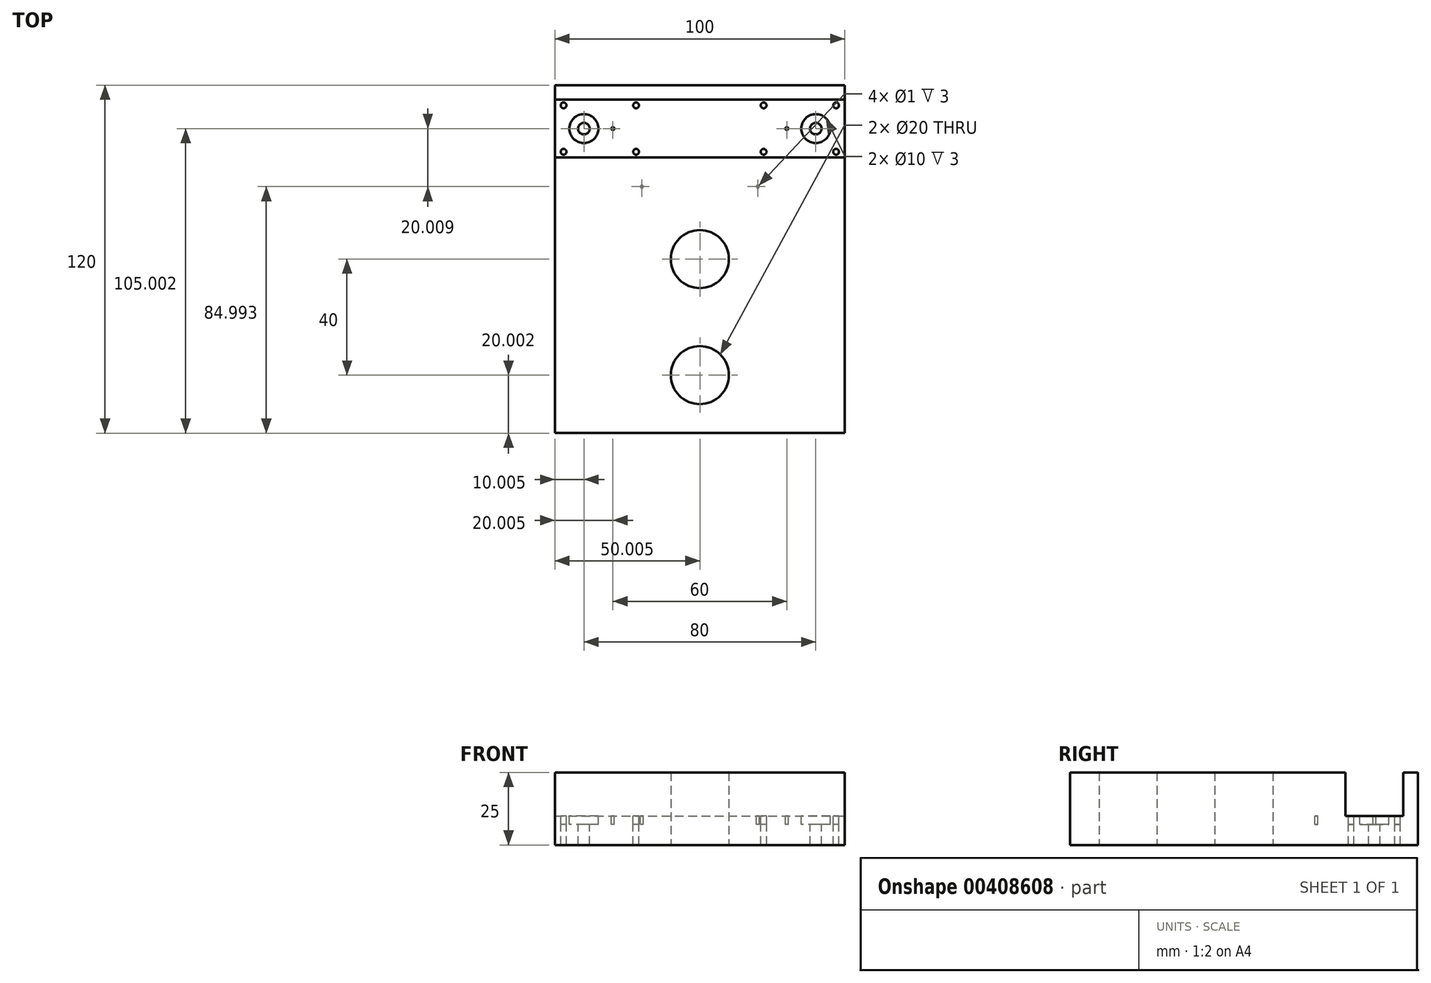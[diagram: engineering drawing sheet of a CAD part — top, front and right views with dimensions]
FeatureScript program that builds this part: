
annotation { "Feature Type Name" : "Feature", "Feature Type Description" : "" }
export const myFeature = defineFeature(function(context is Context, id is Id, definition is map)
    precondition{}
    {
        {
            var Q0;
            Q0=qCreatedBy(makeId("Top.planeOp"),FACE);
            var sketch = newSketch(context, id + "F0", { "sketchPlane" : qUnion([Q0])});
            skLineSegment(sketch, "E0.bottom", {"start": v(-65.16, 65.34) * mm, "end": v(34.84, 65.34) * mm});
            skLineSegment(sketch, "E0.top", {"start": v(-65.16, -54.66) * mm, "end": v(34.84, -54.66) * mm});
            skLineSegment(sketch, "E0.left", {"start": v(-65.16, 65.34) * mm, "end": v(-65.16, -54.66) * mm});
            skLineSegment(sketch, "E0.right", {"start": v(34.84, 65.34) * mm, "end": v(34.84, -54.66) * mm});
            skLineSegment(sketch, "E1", {"start": v(-15.16, 65.34) * mm, "end": v(-15.16, -54.66) * mm, "construction": true});
            skCircle(sketch, "E2", {"center": v(-15.16, 5.34) * mm, "radius": 10 * mm});
            skCircle(sketch, "E3", {"center": v(-15.16, -34.66) * mm, "radius": 10 * mm});
            skSolve(sketch);
        }
        {
            var Q0;
            Q0=makeQuery(id+"F0.imprint","IMPRINT",FACE,{"disambiguationData":[TD([[makeQuery(id+"F0.imprint","IMPRINT",EDGE,{"derivedFrom":sQuery(id+"F0.wireOp",EDGE,"E0.bottom")}),-1.0]])]});
            extrude(context, id + "F1", {"entities" : qUnion([Q0]), "depth" : 25 * mm});
        }
        {
            var Q0;
            Q0=makeQuery(id+"F1.opExtrude","CAP_FACE",FACE,{"disambiguationData":[OSD([sQuery(id+"F0.wireOp",EDGE,"E0.bottom"),sQuery(id+"F0.wireOp",EDGE,"E0.top"),sQuery(id+"F0.wireOp",EDGE,"E0.left"),sQuery(id+"F0.wireOp",EDGE,"E0.right"),sQuery(id+"F0.wireOp",EDGE,"E2"),sQuery(id+"F0.wireOp",EDGE,"E3")])],"isStart":false});
            var sketch = newSketch(context, id + "F2", { "sketchPlane" : qUnion([Q0])});
            skLineSegment(sketch, "E4.bottom", {"start": v(-65.16, 60.34) * mm, "end": v(34.84, 60.34) * mm});
            skLineSegment(sketch, "E4.top", {"start": v(-65.16, 40.34) * mm, "end": v(34.84, 40.34) * mm});
            skLineSegment(sketch, "E4.left", {"start": v(-65.16, 60.34) * mm, "end": v(-65.16, 40.34) * mm});
            skLineSegment(sketch, "E4.right", {"start": v(34.84, 60.34) * mm, "end": v(34.84, 40.34) * mm});
            skSolve(sketch);
        }
        {
            var Q0;
            Q0 = qSketchRegion(id + "F2", true);
            extrude(context, id + "F3", {"entities" : qUnion([Q0]), "operationType" : NewBodyOperationType.REMOVE, "oppositeDirection" : true, "depth" : 15 * mm});
        }
        {
            var Q0;
            Q0=makeQuery(id+"F3.boolean.opBoolean","COPY",FACE,{"derivedFrom":makeQuery(id+"F3.opExtrude","CAP_FACE",FACE,{"disambiguationData":[OSD([sQuery(id+"F2.wireOp",EDGE,"E4.bottom"),sQuery(id+"F2.wireOp",EDGE,"E4.top"),sQuery(id+"F2.wireOp",EDGE,"E4.left"),sQuery(id+"F2.wireOp",EDGE,"E4.right")])],"isStart":false})});
            var sketch = newSketch(context, id + "F4", { "sketchPlane" : qUnion([Q0])});
            skLineSegment(sketch, "E5", {"start": v(-65.16, 50.34) * mm, "end": v(34.84, 50.34) * mm, "construction": true});
            skLineSegment(sketch, "E6", {"start": v(-65.16, 58.34) * mm, "end": v(34.84, 58.34) * mm, "construction": true});
            skLineSegment(sketch, "E7", {"start": v(-15.16, 60.34) * mm, "end": v(-15.16, 40.34) * mm, "construction": true});
            skPoint(sketch, "E8.MirrorP", {"position": v(32.84, 38.34) * mm});
            skPoint(sketch, "E9.MirrorP", {"position": v(7.84, 38.34) * mm});
            skPoint(sketch, "E10.MirrorP", {"position": v(7.84, 22.34) * mm});
            skPoint(sketch, "E11.MirrorP", {"position": v(32.84, 22.34) * mm});
            skPoint(sketch, "E12.MirrorP", {"position": v(24.84, 30.34) * mm});
            skPoint(sketch, "E13.MirrorP", {"position": v(19.84, 30.34) * mm});
            skPoint(sketch, "E14.MirrorP", {"position": v(14.84, 30.34) * mm});
            skCircle(sketch, "E15", {"center": v(-62.16, 58.34) * mm, "radius": 1 * mm});
            skCircle(sketch, "E16", {"center": v(-37.16, 58.34) * mm, "radius": 1 * mm});
            skCircle(sketch, "E17", {"center": v(-55.16, 50.34) * mm, "radius": 5 * mm});
            skCircle(sketch, "E18", {"center": v(-45.16, 50.34) * mm, "radius": 0.5 * mm});
            skCircle(sketch, "E19", {"center": v(-35.16, 30.33) * mm, "radius": 0.5 * mm});
            skCircle(sketch, "E20.MirrorC", {"center": v(-62.16, 42.34) * mm, "radius": 1 * mm});
            skCircle(sketch, "E21.MirrorC", {"center": v(-37.16, 42.34) * mm, "radius": 1 * mm});
            skCircle(sketch, "E22.MirrorC", {"center": v(31.84, 58.34) * mm, "radius": 1 * mm});
            skCircle(sketch, "E23.MirrorC", {"center": v(6.84, 58.34) * mm, "radius": 1 * mm});
            skCircle(sketch, "E24.MirrorC", {"center": v(24.84, 50.34) * mm, "radius": 5 * mm});
            skCircle(sketch, "E25.MirrorC", {"center": v(31.84, 42.34) * mm, "radius": 1 * mm});
            skCircle(sketch, "E26.MirrorC", {"center": v(6.84, 42.34) * mm, "radius": 1 * mm});
            skCircle(sketch, "E27.MirrorC", {"center": v(14.84, 50.34) * mm, "radius": 0.5 * mm});
            skCircle(sketch, "E28.MirrorC", {"center": v(4.84, 30.33) * mm, "radius": 0.5 * mm});
            skSolve(sketch);
        }
        {
            var Q0;
            Q0 = qSketchRegion(id + "F4", true);
            extrude(context, id + "F5", {"entities" : qUnion([Q0]), "operationType" : NewBodyOperationType.REMOVE, "oppositeDirection" : true, "depth" : 3 * mm});
        }
        {
            var Q0;
            Q0=makeQuery(id+"F4.imprint","IMPRINT",FACE,{"disambiguationData":[TD([[makeQuery(id+"F4.imprint","IMPRINT",EDGE,{"derivedFrom":sQuery(id+"F4.wireOp",EDGE,"E17")}),1.0]])]});
            var sketch = newSketch(context, id + "F6", { "sketchPlane" : qUnion([Q0])});
            skCircle(sketch, "E29.0", {"center": v(-55.16, 50.34) * mm, "radius": 5 * mm, "construction": true});
            skCircle(sketch, "E30", {"center": v(-55.16, 50.34) * mm, "radius": 2 * mm});
            skCircle(sketch, "E31.0", {"center": v(24.84, 50.34) * mm, "radius": 5 * mm, "construction": true});
            skCircle(sketch, "E32", {"center": v(24.84, 50.34) * mm, "radius": 2 * mm});
            skCircle(sketch, "E33.0", {"center": v(-62.16, 58.34) * mm, "radius": 1 * mm});
            skCircle(sketch, "E34.0", {"center": v(-37.16, 58.34) * mm, "radius": 1 * mm});
            skCircle(sketch, "E35.0", {"center": v(-37.16, 42.34) * mm, "radius": 1 * mm});
            skCircle(sketch, "E36.0", {"center": v(-62.16, 42.34) * mm, "radius": 1 * mm});
            skCircle(sketch, "E37.0", {"center": v(6.84, 58.34) * mm, "radius": 1 * mm});
            skCircle(sketch, "E38.0", {"center": v(31.84, 58.34) * mm, "radius": 1 * mm});
            skCircle(sketch, "E39.0", {"center": v(31.84, 42.34) * mm, "radius": 1 * mm});
            skCircle(sketch, "E40.0", {"center": v(6.84, 42.34) * mm, "radius": 1 * mm});
            skSolve(sketch);
        }
        {
            var Q0;
            Q0=makeQuery(id+"F6.imprint","IMPRINT",FACE,{"disambiguationData":[TD([[makeQuery(id+"F6.imprint","IMPRINT",EDGE,{"derivedFrom":sQuery(id+"F6.wireOp",EDGE,"E32")}),1.0]])]});
            var Q1;
            Q1=makeQuery(id+"F6.imprint","IMPRINT",FACE,{"disambiguationData":[TD([[makeQuery(id+"F6.imprint","IMPRINT",EDGE,{"derivedFrom":sQuery(id+"F6.wireOp",EDGE,"E39.0")}),1.0]])]});
            var Q2;
            Q2=makeQuery(id+"F6.imprint","IMPRINT",FACE,{"disambiguationData":[TD([[makeQuery(id+"F6.imprint","IMPRINT",EDGE,{"derivedFrom":sQuery(id+"F6.wireOp",EDGE,"E38.0")}),-1.0]])]});
            var Q3;
            Q3=makeQuery(id+"F6.imprint","IMPRINT",FACE,{"disambiguationData":[TD([[makeQuery(id+"F6.imprint","IMPRINT",EDGE,{"derivedFrom":sQuery(id+"F6.wireOp",EDGE,"E40.0")}),1.0]])]});
            var Q4;
            Q4=makeQuery(id+"F6.imprint","IMPRINT",FACE,{"disambiguationData":[TD([[makeQuery(id+"F6.imprint","IMPRINT",EDGE,{"derivedFrom":sQuery(id+"F6.wireOp",EDGE,"E35.0")}),-1.0]])]});
            var Q5;
            Q5=makeQuery(id+"F6.imprint","IMPRINT",FACE,{"disambiguationData":[TD([[makeQuery(id+"F6.imprint","IMPRINT",EDGE,{"derivedFrom":sQuery(id+"F6.wireOp",EDGE,"E36.0")}),-1.0]])]});
            var Q6;
            Q6=makeQuery(id+"F6.imprint","IMPRINT",FACE,{"disambiguationData":[TD([[makeQuery(id+"F6.imprint","IMPRINT",EDGE,{"derivedFrom":sQuery(id+"F6.wireOp",EDGE,"E37.0")}),-1.0]])]});
            var Q7;
            Q7=makeQuery(id+"F6.imprint","IMPRINT",FACE,{"disambiguationData":[TD([[makeQuery(id+"F6.imprint","IMPRINT",EDGE,{"derivedFrom":sQuery(id+"F6.wireOp",EDGE,"E34.0")}),1.0]])]});
            var Q8;
            Q8=makeQuery(id+"F6.imprint","IMPRINT",FACE,{"disambiguationData":[TD([[makeQuery(id+"F6.imprint","IMPRINT",EDGE,{"derivedFrom":sQuery(id+"F6.wireOp",EDGE,"E30")}),1.0]])]});
            var Q9;
            Q9=makeQuery(id+"F6.imprint","IMPRINT",FACE,{"disambiguationData":[TD([[makeQuery(id+"F6.imprint","IMPRINT",EDGE,{"derivedFrom":sQuery(id+"F6.wireOp",EDGE,"E33.0")}),1.0]])]});
            var Q10;
            Q10=sQuery(id+"F6.wireOp",EDGE,"E31.0");
            var Q11;
            Q11=sQuery(id+"F6.wireOp",EDGE,"E29.0");
            extrude(context, id + "F7", {"entities" : qUnion([Q0, Q1, Q2, Q3, Q4, Q5, Q6, Q7, Q8, Q9]), "operationType" : NewBodyOperationType.REMOVE, "surfaceEntities" : qUnion([Q10, Q11]), "oppositeDirection" : true, "depth" : 25 * mm});
        }
    });
